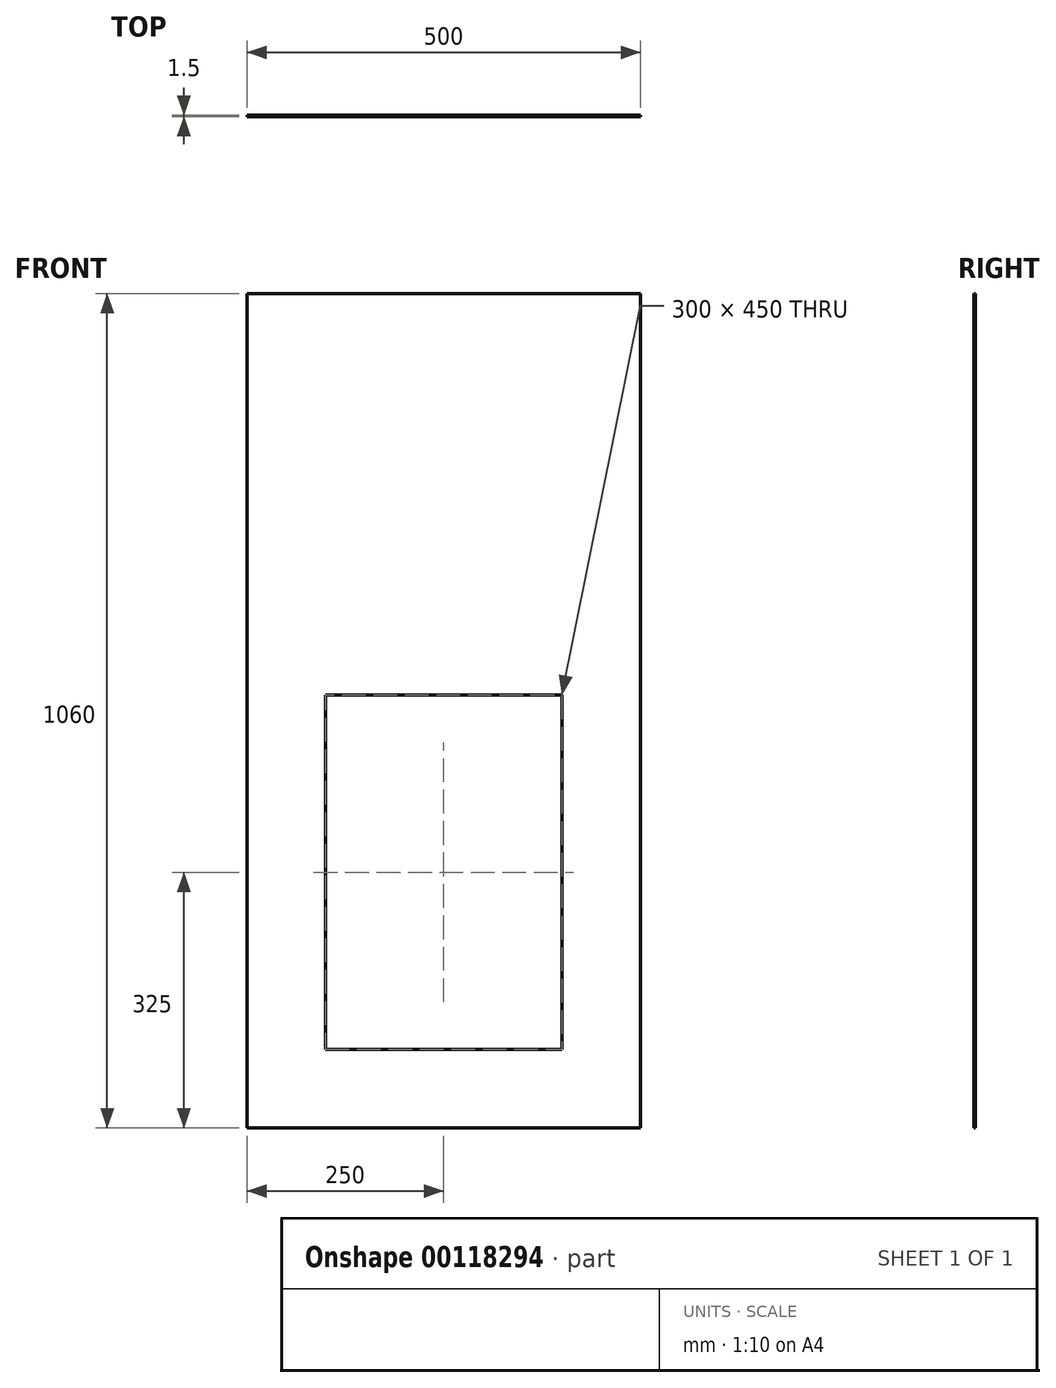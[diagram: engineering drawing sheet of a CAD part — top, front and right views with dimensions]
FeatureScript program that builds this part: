
annotation { "Feature Type Name" : "Feature", "Feature Type Description" : "" }
export const myFeature = defineFeature(function(context is Context, id is Id, definition is map)
    precondition{}
    {
        {
            var Q0;
            Q0=qCreatedBy(makeId("Front.planeOp"),FACE);
            var sketch = newSketch(context, id + "F0", { "sketchPlane" : qUnion([Q0])});
            skLineSegment(sketch, "E0.bottom", {"start": v(250, 530) * mm, "end": v(-250, 530) * mm});
            skLineSegment(sketch, "E0.top", {"start": v(250, -530) * mm, "end": v(-250, -530) * mm});
            skLineSegment(sketch, "E0.left", {"start": v(250, 530) * mm, "end": v(250, -530) * mm});
            skLineSegment(sketch, "E0.right", {"start": v(-250, 530) * mm, "end": v(-250, -530) * mm});
            skPoint(sketch, "E0.middle", {"position": v(0, 0) * mm});
            skSolve(sketch);
        }
        {
            var Q0;
            Q0 = qSketchRegion(id + "F0", true);
            var Q1;
            Q1=makeQuery(id+"F0.imprint","IMPRINT",FACE,{"disambiguationData":[TD([[makeQuery(id+"F0.imprint","IMPRINT",EDGE,{"derivedFrom":sQuery(id+"F0.wireOp",EDGE,"E0.bottom")}),1.0]])]});
            extrude(context, id + "F1", {"entities" : qUnion([Q0, Q1]), "depth" : 1.5 * mm});
        }
        {
            var Q0;
            Q0=makeQuery(id+"F1.opExtrude","CAP_FACE",FACE,{"disambiguationData":[OSD([sQuery(id+"F0.wireOp",EDGE,"E0.bottom"),sQuery(id+"F0.wireOp",EDGE,"E0.top"),sQuery(id+"F0.wireOp",EDGE,"E0.left"),sQuery(id+"F0.wireOp",EDGE,"E0.right")])],"isStart":false});
            var sketch = newSketch(context, id + "F2", { "sketchPlane" : qUnion([Q0])});
            skLineSegment(sketch, "E1.bottom", {"start": v(-250, -530) * mm, "end": v(250, -530) * mm});
            skLineSegment(sketch, "E1.top", {"start": v(-250, 70) * mm, "end": v(250, 70) * mm});
            skLineSegment(sketch, "E1.left", {"start": v(-250, -530) * mm, "end": v(-250, 70) * mm});
            skLineSegment(sketch, "E1.right", {"start": v(250, -530) * mm, "end": v(250, 70) * mm});
            skLineSegment(sketch, "E2.0", {"start": v(-150, -430) * mm, "end": v(-150, -30) * mm});
            skLineSegment(sketch, "E2.1", {"start": v(-150, -430) * mm, "end": v(150, -430) * mm});
            skLineSegment(sketch, "E2.2", {"start": v(150, -430) * mm, "end": v(150, -30) * mm});
            skLineSegment(sketch, "E2.3", {"start": v(-150, -30) * mm, "end": v(150, -30) * mm});
            skLineSegment(sketch, "E3.top", {"start": v(-150, 20) * mm, "end": v(150, 20) * mm});
            skLineSegment(sketch, "E3.left", {"start": v(-150, -30) * mm, "end": v(-150, 20) * mm});
            skLineSegment(sketch, "E3.right", {"start": v(150, -30) * mm, "end": v(150, 20) * mm});
            skSolve(sketch);
        }
        {
            var Q0;
            Q0=makeQuery(id+"F2.imprint","IMPRINT",FACE,{"disambiguationData":[TD([[makeQuery(id+"F2.imprint","IMPRINT",EDGE,{"derivedFrom":sQuery(id+"F2.wireOp",EDGE,"E2.3")}),1.0]])]});
            var Q1;
            Q1=makeQuery(id+"F2.imprint","IMPRINT",FACE,{"disambiguationData":[TD([[makeQuery(id+"F2.imprint","IMPRINT",EDGE,{"derivedFrom":sQuery(id+"F2.wireOp",EDGE,"E2.0")}),-1.0]])]});
            extrude(context, id + "F3", {"entities" : qUnion([Q0, Q1]), "operationType" : NewBodyOperationType.REMOVE, "oppositeDirection" : true, "depth" : 25 * mm});
        }
    });
